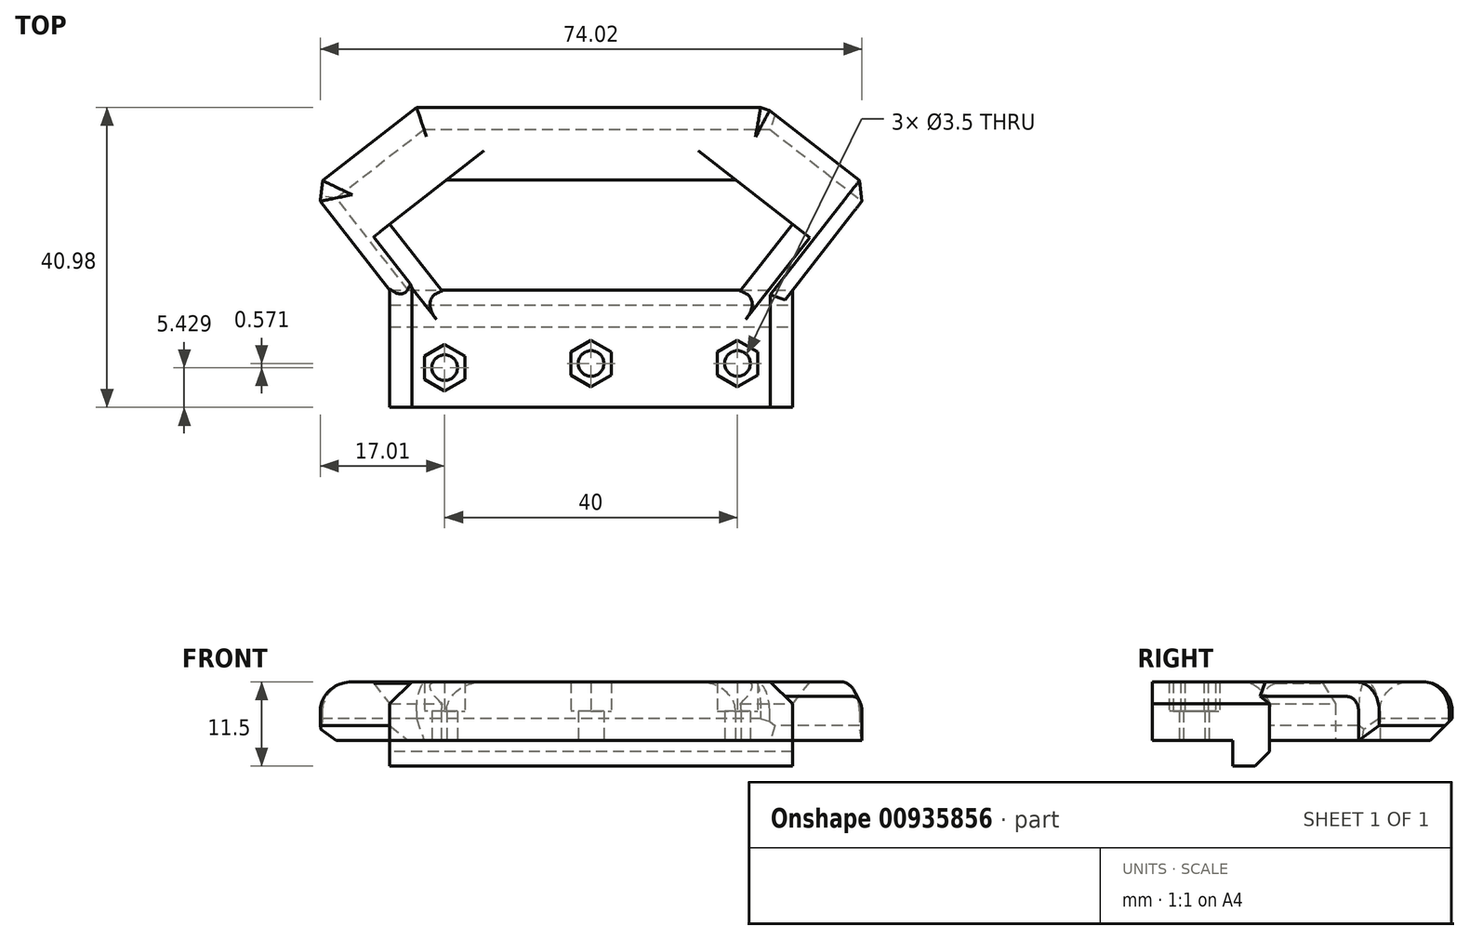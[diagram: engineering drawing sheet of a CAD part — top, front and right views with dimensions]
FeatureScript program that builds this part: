
annotation { "Feature Type Name" : "Feature", "Feature Type Description" : "" }
export const myFeature = defineFeature(function(context is Context, id is Id, definition is map)
    precondition{}
    {
        {
            var Q0;
            Q0=qCreatedBy(makeId("Top.planeOp"),FACE);
            var sketch = newSketch(context, id + "F0", { "sketchPlane" : qUnion([Q0])});
            skLineSegment(sketch, "E0.bottom", {"start": v(-27.5, 8) * mm, "end": v(27.5, 8) * mm});
            skLineSegment(sketch, "E0.top", {"start": v(-27.5, -8) * mm, "end": v(27.5, -8) * mm});
            skLineSegment(sketch, "E0.left", {"start": v(-27.5, 8) * mm, "end": v(-27.5, -8) * mm});
            skLineSegment(sketch, "E0.right", {"start": v(27.5, 8) * mm, "end": v(27.5, -8) * mm});
            skPoint(sketch, "E0.middle", {"position": v(0, 0) * mm});
            skLineSegment(sketch, "E1", {"start": v(-27.5, 3) * mm, "end": v(27.5, 3) * mm});
            skCircle(sketch, "E2.cCircle", {"center": v(0, -2) * mm, "radius": 2.75 * mm, "construction": true});
            skPoint(sketch, "E2.cCircle.centerSnap0", {"position": v(0, -8) * mm});
            skLineSegment(sketch, "E2.0", {"start": v(-2.75, -3.59) * mm, "end": v(-2.75, -0.41) * mm});
            skLineSegment(sketch, "E2.1", {"start": v(-2.75, -0.41) * mm, "end": v(0, 1.18) * mm});
            skLineSegment(sketch, "E2.2", {"start": v(0, 1.18) * mm, "end": v(2.75, -0.41) * mm});
            skLineSegment(sketch, "E2.3", {"start": v(2.75, -0.41) * mm, "end": v(2.75, -3.59) * mm});
            skLineSegment(sketch, "E2.4", {"start": v(2.75, -3.59) * mm, "end": v(0, -5.18) * mm});
            skLineSegment(sketch, "E2.5", {"start": v(0, -5.18) * mm, "end": v(-2.75, -3.59) * mm});
            skPoint(sketch, "E2.0.midPoint", {"position": v(-2.75, -2) * mm});
            skCircle(sketch, "E3", {"center": v(0, -2) * mm, "radius": 1.75 * mm});
            skPoint(sketch, "E4.0.midPoint", {"position": v(-10.58, 0) * mm});
            skCircle(sketch, "E5.cCircle", {"center": v(20, -2) * mm, "radius": 2.75 * mm, "construction": true});
            skLineSegment(sketch, "E5.0", {"start": v(17.25, -0.41) * mm, "end": v(20, 1.18) * mm});
            skLineSegment(sketch, "E5.1", {"start": v(20, 1.18) * mm, "end": v(22.75, -0.41) * mm});
            skLineSegment(sketch, "E5.2", {"start": v(22.75, -0.41) * mm, "end": v(22.75, -3.59) * mm});
            skLineSegment(sketch, "E5.3", {"start": v(22.75, -3.59) * mm, "end": v(20, -5.18) * mm});
            skLineSegment(sketch, "E5.4", {"start": v(20, -5.18) * mm, "end": v(17.25, -3.59) * mm});
            skLineSegment(sketch, "E5.5", {"start": v(17.25, -3.59) * mm, "end": v(17.25, -0.41) * mm});
            skPoint(sketch, "E5.0.midPoint", {"position": v(18.63, 0.38) * mm});
            skCircle(sketch, "E6", {"center": v(20, -2) * mm, "radius": 1.75 * mm});
            skCircle(sketch, "E7.cCircle", {"center": v(-20, -2.57) * mm, "radius": 2.75 * mm, "construction": true});
            skLineSegment(sketch, "E7.0", {"start": v(-17.25, -0.98) * mm, "end": v(-17.25, -4.16) * mm});
            skLineSegment(sketch, "E7.1", {"start": v(-17.25, -4.16) * mm, "end": v(-20, -5.75) * mm});
            skLineSegment(sketch, "E7.2", {"start": v(-20, -5.75) * mm, "end": v(-22.75, -4.16) * mm});
            skLineSegment(sketch, "E7.3", {"start": v(-22.75, -4.16) * mm, "end": v(-22.75, -0.98) * mm});
            skLineSegment(sketch, "E7.4", {"start": v(-22.75, -0.98) * mm, "end": v(-20, 0.6) * mm});
            skLineSegment(sketch, "E7.5", {"start": v(-20, 0.6) * mm, "end": v(-17.25, -0.98) * mm});
            skPoint(sketch, "E7.0.midPoint", {"position": v(-17.25, -2.57) * mm});
            skCircle(sketch, "E8", {"center": v(-20, -2.57) * mm, "radius": 1.75 * mm});
            skLineSegment(sketch, "E9", {"start": v(-27.5, 8) * mm, "end": v(-38.24, 21.75) * mm});
            skLineSegment(sketch, "E10", {"start": v(-38.24, 21.75) * mm, "end": v(-23.86, 32.98) * mm});
            skLineSegment(sketch, "E11", {"start": v(-23.86, 32.98) * mm, "end": v(0, 32.98) * mm});
            skLineSegment(sketch, "E12.MirrorCS", {"start": v(38.24, 21.75) * mm, "end": v(23.86, 32.98) * mm});
            skLineSegment(sketch, "E13.MirrorCS", {"start": v(23.86, 32.98) * mm, "end": v(0, 32.98) * mm});
            skLineSegment(sketch, "E14", {"start": v(38.24, 21.75) * mm, "end": v(27.5, 8) * mm});
            skLineSegment(sketch, "E15", {"start": v(-20.46, 8) * mm, "end": v(-27.5, 17.02) * mm});
            skLineSegment(sketch, "E16", {"start": v(-27.5, 17.02) * mm, "end": v(-19.74, 23.08) * mm});
            skLineSegment(sketch, "E17", {"start": v(-19.74, 23.08) * mm, "end": v(0, 23.08) * mm});
            skLineSegment(sketch, "E18.MirrorCS", {"start": v(27.5, 8) * mm, "end": v(38.24, 21.75) * mm});
            skLineSegment(sketch, "E19.MirrorCS", {"start": v(27.5, 17.02) * mm, "end": v(19.74, 23.08) * mm});
            skLineSegment(sketch, "E20.MirrorCS", {"start": v(19.74, 23.08) * mm, "end": v(0, 23.08) * mm});
            skLineSegment(sketch, "E21.MirrorCS", {"start": v(20.46, 8) * mm, "end": v(27.5, 17.02) * mm});
            skSolve(sketch);
        }
        {
            var Q0;
            {var subQ0=sQuery(id+"F0.wireOp",EDGE,"E0.bottom");Q0=makeQuery(id+"F0.imprint","IMPRINT",FACE,{"disambiguationData":[TD([[makeQuery(id+"F0.imprint","IMPRINT",EDGE,{"derivedFrom":subQ0}),-1.0]])]});}
            var Q1;
            {var subQ18=sQuery(id+"F0.wireOp",EDGE,"E0.top");Q1=makeQuery(id+"F0.imprint","IMPRINT",FACE,{"disambiguationData":[TD([[makeQuery(id+"F0.imprint","IMPRINT",EDGE,{"derivedFrom":subQ18}),1.0]])]});}
            extrude(context, id + "F1", {"entities" : qUnion([Q0, Q1]), "depth" : 8 * mm, "offsetDistance" : 25 * mm});
        }
        {
            var Q0;
            Q0=makeQuery(id+"F0.imprint","IMPRINT",FACE,{"disambiguationData":[TD([[makeQuery(id+"F0.imprint","IMPRINT",EDGE,{"derivedFrom":sQuery(id+"F0.wireOp",EDGE,"E2.0")}),-1.0]])]});
            var Q1;
            Q1=makeQuery(id+"F0.imprint","IMPRINT",FACE,{"disambiguationData":[TD([[makeQuery(id+"F0.imprint","IMPRINT",EDGE,{"derivedFrom":sQuery(id+"F0.wireOp",EDGE,"E7.0")}),-1.0]])]});
            var Q2;
            Q2=makeQuery(id+"F0.imprint","IMPRINT",FACE,{"disambiguationData":[TD([[makeQuery(id+"F0.imprint","IMPRINT",EDGE,{"derivedFrom":sQuery(id+"F0.wireOp",EDGE,"E5.0")}),-1.0]])]});
            extrude(context, id + "F2", {"entities" : qUnion([Q0, Q1, Q2]), "operationType" : NewBodyOperationType.ADD, "depth" : 4 * mm, "offsetDistance" : 25 * mm});
        }
        {
            var Q0;
            {var subQ0=sQuery(id+"F0.wireOp",EDGE,"E0.bottom");Q0=makeQuery(id+"F0.imprint","IMPRINT",FACE,{"disambiguationData":[TD([[makeQuery(id+"F0.imprint","IMPRINT",EDGE,{"derivedFrom":subQ0}),-1.0]])]});}
            extrude(context, id + "F3", {"entities" : qUnion([Q0]), "operationType" : NewBodyOperationType.ADD, "oppositeDirection" : true, "depth" : 3.5 * mm, "offsetDistance" : 25 * mm});
        }
        {
            var Q0;
            {var subQ1=sQuery(id+"F0.wireOp",EDGE,"E0.bottom");Q0=makeQuery(id+"F0.imprint","IMPRINT",FACE,{"disambiguationData":[TD([[makeQuery(id+"F0.imprint","IMPRINT",EDGE,{"derivedFrom":subQ1}),1.0]])]});}
            extrude(context, id + "F4", {"entities" : qUnion([Q0]), "operationType" : NewBodyOperationType.ADD, "depth" : 8 * mm, "offsetDistance" : 25 * mm});
        }
        {
            var Q0;
            Q0=makeQuery(id+"F4.opExtrude","CAP_EDGE",EDGE,{"disambiguationData":[OSD([sQuery(id+"F0.wireOp",EDGE,"E11"),sQuery(id+"F0.wireOp",EDGE,"E13.MirrorCS")])],"isStart":false});
            var Q1;
            Q1=makeQuery(id+"F4.opExtrude","CAP_EDGE",EDGE,{"disambiguationData":[OSD([sQuery(id+"F0.wireOp",EDGE,"E10")])],"isStart":false});
            var Q2;
            Q2=makeQuery(id+"F4.opExtrude","CAP_EDGE",EDGE,{"disambiguationData":[OSD([sQuery(id+"F0.wireOp",EDGE,"E9")])],"isStart":false});
            var Q3;
            Q3=makeQuery(id+"F4.opExtrude","CAP_EDGE",EDGE,{"disambiguationData":[OSD([sQuery(id+"F0.wireOp",EDGE,"E12.MirrorCS")])],"isStart":false});
            var Q4;
            Q4=makeQuery(id+"F4.opExtrude","CAP_EDGE",EDGE,{"disambiguationData":[OSD([sQuery(id+"F0.wireOp",EDGE,"E17"),sQuery(id+"F0.wireOp",EDGE,"E20.MirrorCS")])],"isStart":false});
            var Q5;
            Q5=makeQuery(id+"F1.opExtrude","CAP_EDGE",EDGE,{"disambiguationData":[OSD([sQuery(id+"F0.wireOp",EDGE,"E0.bottom")])],"isStart":false});
            fillet(context, id + "F5", {"entities" : qUnion([Q0, Q1, Q2, Q3, Q4, Q5]), "radius" : 4 * mm, "tangentPropagation" : true, "allowEdgeOverflow" : false});
        }
        {
            var Q0;
            Q0=makeQuery(id+"F4.opExtrude","SWEPT_FACE",FACE,{"disambiguationData":[OSD([sQuery(id+"F0.wireOp",EDGE,"HIhc4do8-B8tj-e9a0-O9ur-uNlmLRdUL1Do")])]});
            var Q1;
            {var subQ0=sQuery(id+"F0.wireOp",EDGE,"nJX3Etnb-P5HZ-u3x9-83od-tfGPIH08Xn17");Q1=makeQuery(id+"F4.opExtrude","SWEPT_FACE",FACE,{"disambiguationData":[OSD([subQ0]),TDD([makeQuery(id+"F0.imprint","IMPRINT",EDGE,{"disambiguationData":[TD([[makeQuery(id+"F0.imprint","INTERSECT",VERTEX,{"disambiguationData":[OD(1.0)],"derivedFrom":[subQ0,sQuery(id+"F0.wireOp",EDGE,"b542f90a-a1cc-4908-bcdd-dd524b4577f80.MirrorC")]}),-1.0]])],"derivedFrom":subQ0})])]});}
            var Q2;
            Q2=makeQuery(id+"F4.opExtrude","CAP_EDGE",EDGE,{"disambiguationData":[OSD([sQuery(id+"F0.wireOp",EDGE,"E18.MirrorCS")])],"isStart":true});
            var Q3;
            Q3=makeQuery(id+"F4.opExtrude","CAP_EDGE",EDGE,{"disambiguationData":[OSD([sQuery(id+"F0.wireOp",EDGE,"E11"),sQuery(id+"F0.wireOp",EDGE,"E13.MirrorCS")])],"isStart":true});
            var Q4;
            Q4=makeQuery(id+"F4.opExtrude","CAP_EDGE",EDGE,{"disambiguationData":[OSD([sQuery(id+"F0.wireOp",EDGE,"E10")])],"isStart":true});
            var Q5;
            Q5=makeQuery(id+"F4.opExtrude","CAP_EDGE",EDGE,{"disambiguationData":[OSD([sQuery(id+"F0.wireOp",EDGE,"E15")])],"isStart":false});
            var Q6;
            Q6=makeQuery(id+"F4.opExtrude","CAP_EDGE",EDGE,{"disambiguationData":[OSD([sQuery(id+"F0.wireOp",EDGE,"E21.MirrorCS")])],"isStart":false});
            chamfer(context, id + "F6", {"entities" : qUnion([Q0, Q1, Q2, Q3, Q4, Q5, Q6]), "width" : 3 * mm, "tangentPropagation" : true});
        }
        {
            var Q0;
            Q0=makeQuery(id+"F1.opExtrude","CAP_EDGE",EDGE,{"disambiguationData":[OSD([sQuery(id+"F0.wireOp",EDGE,"E0.left")])],"isStart":false});
            var Q1;
            Q1=makeQuery(id+"F1.opExtrude","CAP_EDGE",EDGE,{"disambiguationData":[OSD([sQuery(id+"F0.wireOp",EDGE,"E0.right")])],"isStart":false});
            chamfer(context, id + "F7", {"entities" : qUnion([Q0, Q1]), "width" : 3 * mm, "tangentPropagation" : true});
        }
        {
            var Q0;
            Q0=makeQuery(id+"F4.opExtrude","SWEPT_EDGE",EDGE,{"disambiguationData":[OSD([sQuery(id+"F0.wireOp",EDGE,"E9"),sQuery(id+"F0.wireOp",EDGE,"E10")])]});
            var Q1;
            Q1=makeQuery(id+"F4.opExtrude","SWEPT_EDGE",EDGE,{"disambiguationData":[OSD([sQuery(id+"F0.wireOp",EDGE,"E12.MirrorCS"),sQuery(id+"F0.wireOp",EDGE,"E18.MirrorCS")])]});
            var Q2;
            Q2=makeQuery(id+"F4.opExtrude","CAP_EDGE",EDGE,{"disambiguationData":[OSD([sQuery(id+"F0.wireOp",EDGE,"E11"),sQuery(id+"F0.wireOp",EDGE,"E13.MirrorCS")])],"isStart":true});
            var Q3;
            Q3=makeQuery(id+"F4.opExtrude","CAP_EDGE",EDGE,{"disambiguationData":[OSD([sQuery(id+"F0.wireOp",EDGE,"E12.MirrorCS")])],"isStart":true});
            var Q4;
            Q4=makeQuery(id+"F4.opExtrude","CAP_EDGE",EDGE,{"disambiguationData":[OSD([sQuery(id+"F0.wireOp",EDGE,"E18.MirrorCS")])],"isStart":true});
            var Q5;
            Q5=makeQuery(id+"F4.opExtrude","CAP_EDGE",EDGE,{"disambiguationData":[OSD([sQuery(id+"F0.wireOp",EDGE,"E9")])],"isStart":true});
            var Q6;
            Q6=makeQuery(id+"F4.opExtrude","CAP_EDGE",EDGE,{"disambiguationData":[OSD([sQuery(id+"F0.wireOp",EDGE,"E10")])],"isStart":true});
            var Q7;
            Q7=makeQuery(id+"F3.opExtrude","CAP_EDGE",EDGE,{"disambiguationData":[OSD([sQuery(id+"F0.wireOp",EDGE,"E0.bottom")])],"isStart":false});
            chamfer(context, id + "F8", {"entities" : qUnion([Q0, Q1, Q2, Q3, Q4, Q5, Q6, Q7]), "width" : 2 * mm, "tangentPropagation" : true});
        }
    });
